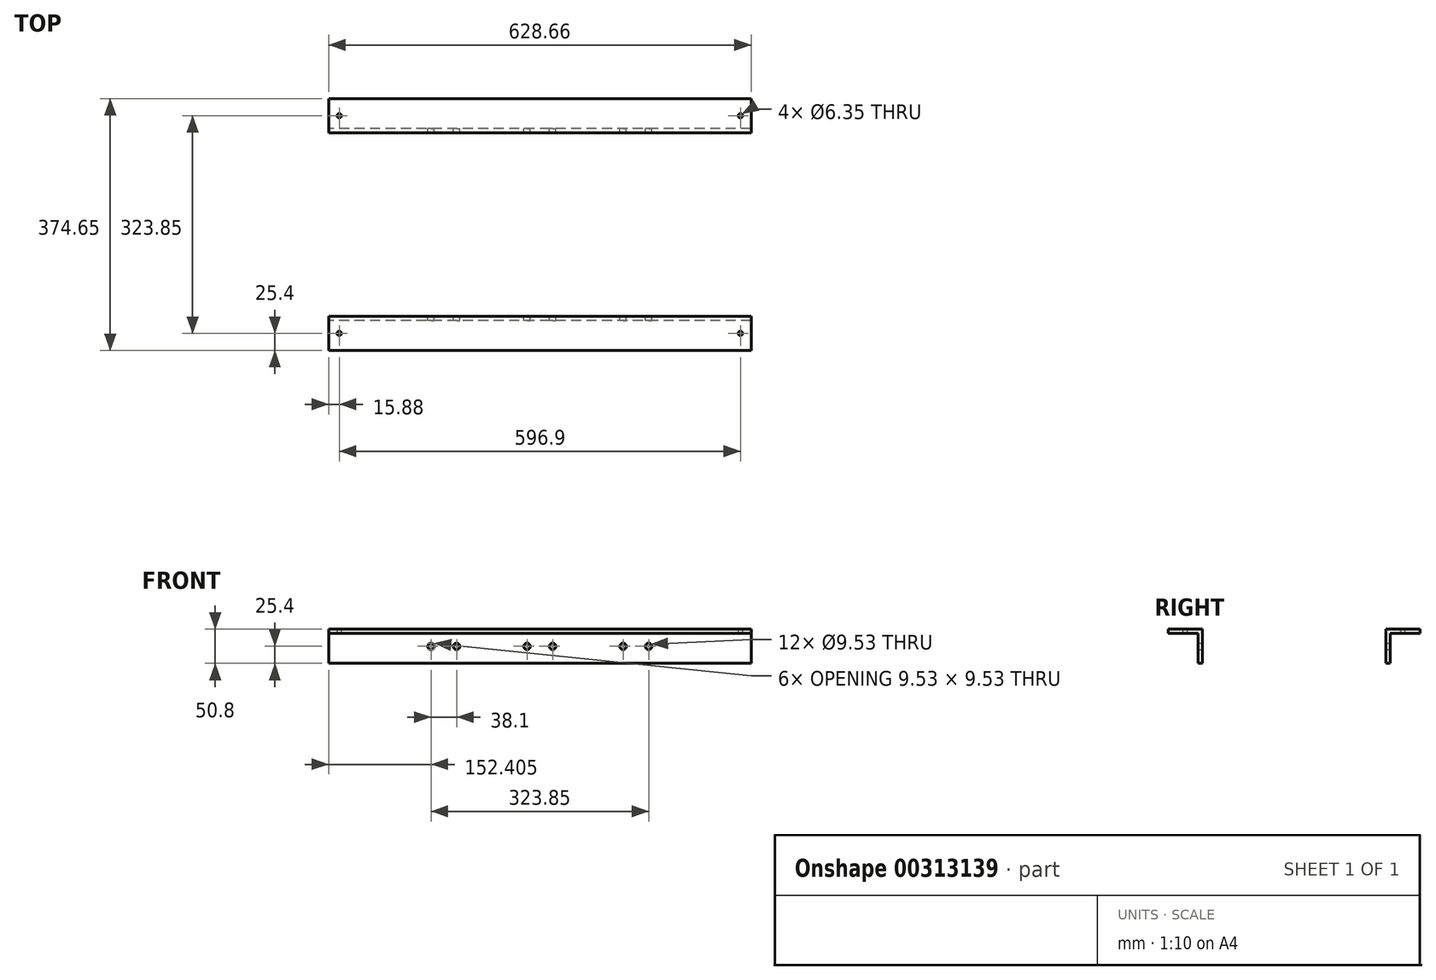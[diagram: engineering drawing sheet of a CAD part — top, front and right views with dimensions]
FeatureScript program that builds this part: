
annotation { "Feature Type Name" : "Feature", "Feature Type Description" : "" }
export const myFeature = defineFeature(function(context is Context, id is Id, definition is map)
    precondition{}
    {
        {
            var Q0;
            Q0=qCreatedBy(makeId("Right.planeOp"),FACE);
            var sketch = newSketch(context, id + "F0", { "sketchPlane" : qUnion([Q0])});
            skLineSegment(sketch, "E0", {"start": v(0, 0) * mm, "end": v(0, 44.45) * mm});
            skLineSegment(sketch, "E1", {"start": v(0, 44.45) * mm, "end": v(-44.45, 44.45) * mm});
            skLineSegment(sketch, "E2", {"start": v(-44.45, 44.45) * mm, "end": v(-44.45, 50.8) * mm});
            skLineSegment(sketch, "E3", {"start": v(-44.45, 50.8) * mm, "end": v(6.35, 50.8) * mm});
            skLineSegment(sketch, "E4", {"start": v(6.35, 50.8) * mm, "end": v(6.35, 0) * mm});
            skLineSegment(sketch, "E5", {"start": v(6.35, 0) * mm, "end": v(0, 0) * mm});
            skLineSegment(sketch, "E6", {"start": v(6.35, 50.8) * mm, "end": v(142.88, 50.8) * mm, "construction": true});
            skLineSegment(sketch, "E7", {"start": v(142.88, 50.8) * mm, "end": v(142.88, 0) * mm, "construction": true});
            skLineSegment(sketch, "E8.MirrorCS", {"start": v(330.2, 50.8) * mm, "end": v(279.4, 50.8) * mm});
            skLineSegment(sketch, "E9.MirrorCS", {"start": v(279.4, 0) * mm, "end": v(285.75, 0) * mm});
            skLineSegment(sketch, "E10.MirrorCS", {"start": v(279.4, 50.8) * mm, "end": v(279.4, 0) * mm});
            skLineSegment(sketch, "E11.MirrorCS", {"start": v(330.2, 44.45) * mm, "end": v(330.2, 50.8) * mm});
            skLineSegment(sketch, "E12.MirrorCS", {"start": v(285.75, 44.45) * mm, "end": v(330.2, 44.45) * mm});
            skLineSegment(sketch, "E13.MirrorCS", {"start": v(285.75, 0) * mm, "end": v(285.75, 44.45) * mm});
            skSolve(sketch);
        }
        {
            var Q0;
            Q0 = qSketchRegion(id + "F0", true);
            extrude(context, id + "F1", {"entities" : qUnion([Q0]), "endBound" : BoundingType.SYMMETRIC, "depth" : 628.65 * mm});
        }
        {
            var Q0;
            Q0=makeQuery(id+"F1.opExtrude","SWEPT_FACE",FACE,{"disambiguationData":[OSD([sQuery(id+"F0.wireOp",EDGE,"E3")])]});
            var sketch = newSketch(context, id + "F2", { "sketchPlane" : qUnion([Q0])});
            skCircle(sketch, "E14", {"center": v(-298.45, -19.05) * mm, "radius": 3.18 * mm});
            skPoint(sketch, "E14.centerSnap0", {"position": v(-314.33, -19.05) * mm});
            skCircle(sketch, "E15", {"center": v(298.45, -19.05) * mm, "radius": 3.18 * mm});
            skPoint(sketch, "E16.0.1.0", {"position": v(-314.33, 304.8) * mm});
            skCircle(sketch, "E16.0.1.1", {"center": v(-298.45, 304.8) * mm, "radius": 3.18 * mm});
            skCircle(sketch, "E16.0.1.5", {"center": v(298.45, 304.8) * mm, "radius": 3.18 * mm});
            skLineSegment(sketch, "E16.direction1", {"start": v(-314.33, -19.05) * mm, "end": v(-298.45, -19.05) * mm, "construction": true});
            skLineSegment(sketch, "E16.direction2", {"start": v(-314.33, -19.05) * mm, "end": v(-314.33, 304.8) * mm, "construction": true});
            skSolve(sketch);
        }
        {
            var Q0;
            Q0 = qSketchRegion(id + "F2", true);
            extrude(context, id + "F3", {"entities" : qUnion([Q0]), "operationType" : NewBodyOperationType.REMOVE, "endBound" : BoundingType.THROUGH_ALL, "oppositeDirection" : true, "depth" : 25.4 * mm});
        }
        {
            var Q0;
            Q0=makeQuery(id+"F1.opExtrude","SWEPT_FACE",FACE,{"disambiguationData":[OSD([sQuery(id+"F0.wireOp",EDGE,"E4")])]});
            var sketch = newSketch(context, id + "F4", { "sketchPlane" : qUnion([Q0])});
            skCircle(sketch, "E17", {"center": v(123.83, 25.4) * mm, "radius": 4.76 * mm});
            skPoint(sketch, "E17.centerSnap0", {"position": v(-314.33, 25.4) * mm});
            skCircle(sketch, "E18", {"center": v(161.93, 25.4) * mm, "radius": 4.76 * mm});
            skCircle(sketch, "E19.1.0.0", {"center": v(19.05, 25.4) * mm, "radius": 4.76 * mm});
            skCircle(sketch, "E19.1.0.1", {"center": v(-19.05, 25.4) * mm, "radius": 4.76 * mm});
            skCircle(sketch, "E19.2.0.0", {"center": v(-123.82, 25.4) * mm, "radius": 4.76 * mm});
            skCircle(sketch, "E19.2.0.1", {"center": v(-161.92, 25.4) * mm, "radius": 4.76 * mm});
            skLineSegment(sketch, "E19.direction1", {"start": v(123.83, 25.4) * mm, "end": v(-19.05, 25.4) * mm, "construction": true});
            skSolve(sketch);
        }
        {
            var Q0;
            Q0 = qSketchRegion(id + "F4", true);
            extrude(context, id + "F5", {"entities" : qUnion([Q0]), "operationType" : NewBodyOperationType.REMOVE, "endBound" : BoundingType.THROUGH_ALL, "oppositeDirection" : true, "depth" : 25.4 * mm, "hasSecondDirection" : true, "secondDirectionBound" : SecondDirectionBoundingType.THROUGH_ALL, "secondDirectionOppositeDirection" : false, "secondDirectionDepth" : 25.4 * mm});
        }
    });
